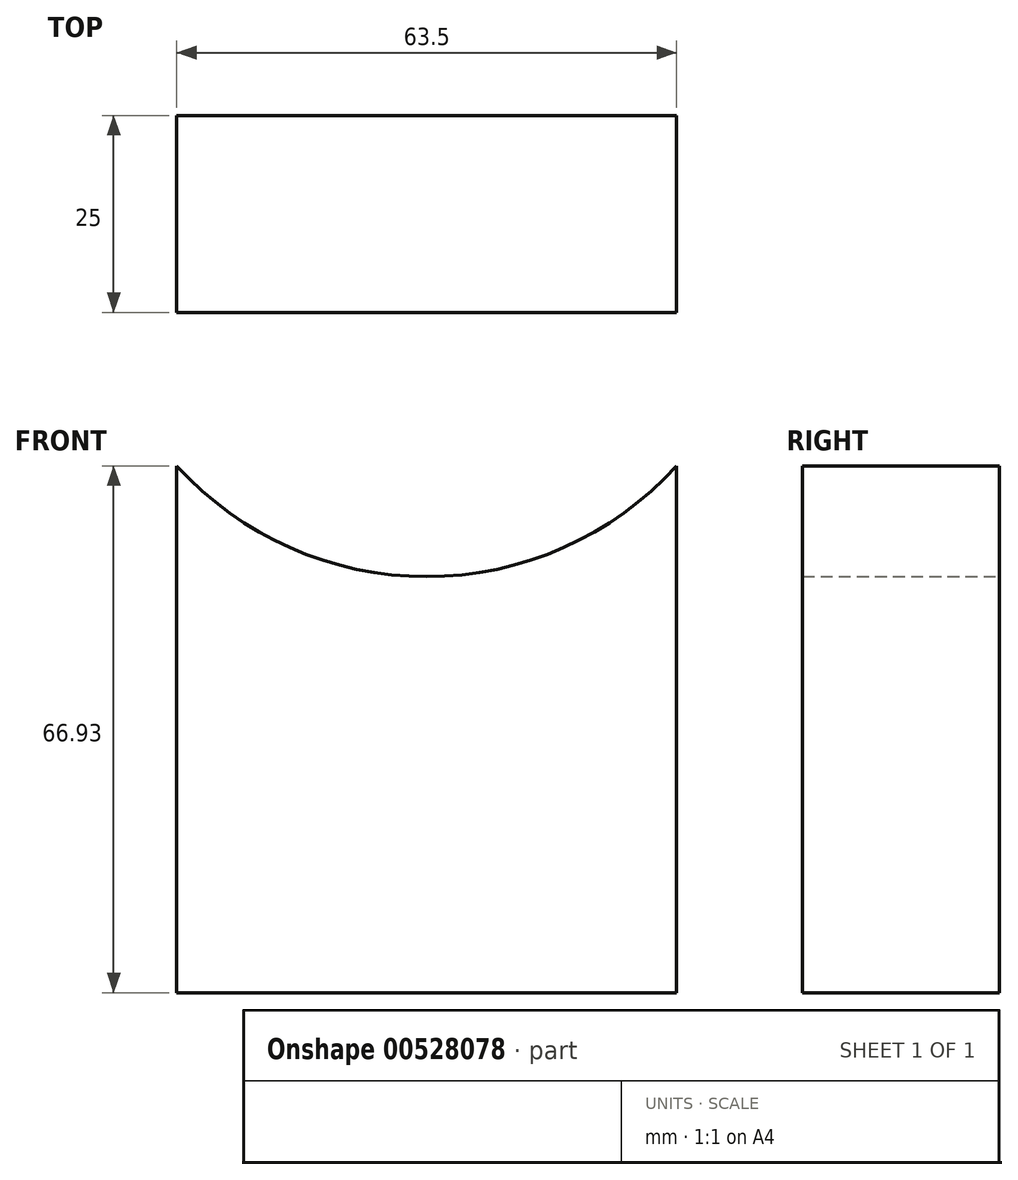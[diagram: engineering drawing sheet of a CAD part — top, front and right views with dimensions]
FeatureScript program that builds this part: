
annotation { "Feature Type Name" : "Feature", "Feature Type Description" : "" }
export const myFeature = defineFeature(function(context is Context, id is Id, definition is map)
    precondition{}
    {
        {
            var Q0;
            Q0=qCreatedBy(makeId("Front.planeOp"),FACE);
            var sketch = newSketch(context, id + "F0", { "sketchPlane" : qUnion([Q0])});
            skLineSegment(sketch, "E0.bottom", {"start": v(185.68, -41) * mm, "end": v(122.18, -41) * mm});
            skLineSegment(sketch, "E0.left", {"start": v(185.68, -41) * mm, "end": v(185.68, 25.92) * mm});
            skLineSegment(sketch, "E0.right", {"start": v(122.18, -41) * mm, "end": v(122.18, 25.92) * mm});
            skPoint(sketch, "E0.middle", {"position": v(153.93, -7.55) * mm});
            skArc(sketch, "E1", {"start": v(122.18, 25.92) * mm, "mid": v(153.93, 11.84) * mm, "end": v(185.68, 25.92) * mm});
            skSolve(sketch);
        }
        {
            var Q0;
            Q0 = qSketchRegion(id + "F0", true);
            extrude(context, id + "F1", {"entities" : qUnion([Q0]), "depth" : 25 * mm, "offsetDistance" : 25 * mm});
        }
    });
